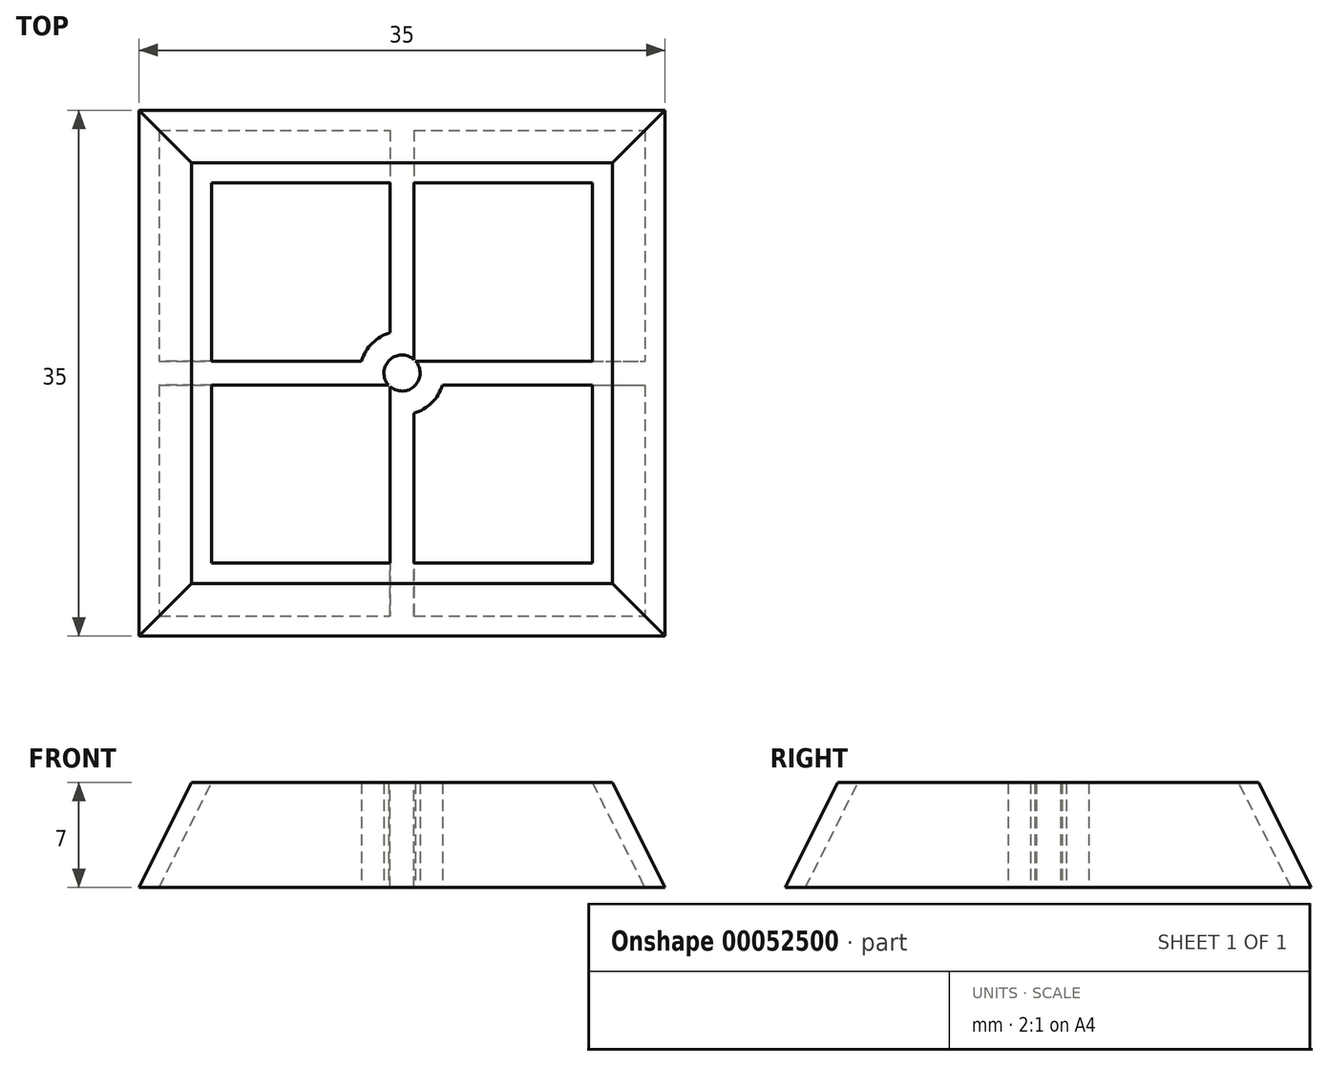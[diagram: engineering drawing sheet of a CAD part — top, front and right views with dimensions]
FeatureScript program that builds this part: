
annotation { "Feature Type Name" : "Feature", "Feature Type Description" : "" }
export const myFeature = defineFeature(function(context is Context, id is Id, definition is map)
    precondition{}
    {
        {
            var Q0;
            Q0=qCreatedBy(makeId("Top.planeOp"),FACE);
            var sketch = newSketch(context, id + "F0", { "sketchPlane" : qUnion([Q0])});
            skLineSegment(sketch, "E0.rect.bottom", {"start": v(-17.5, 17.5) * mm, "end": v(17.5, 17.5) * mm});
            skLineSegment(sketch, "E0.rect.top", {"start": v(-17.5, -17.5) * mm, "end": v(17.5, -17.5) * mm});
            skLineSegment(sketch, "E0.rect.left", {"start": v(-17.5, 17.5) * mm, "end": v(-17.5, -17.5) * mm});
            skLineSegment(sketch, "E0.rect.right", {"start": v(17.5, 17.5) * mm, "end": v(17.5, -17.5) * mm});
            skPoint(sketch, "E0.rect.middle", {"position": v(0, 0) * mm});
            skSolve(sketch);
        }
        {
            var Q0;
            Q0=qCreatedBy(makeId("Top.planeOp"),FACE);
            cPlane(context, id + "F1", {"entities" : qUnion([Q0]), "cplaneType" : CPlaneType.OFFSET, "offset" : 7 * mm, "width" : 150 * mm, "height" : 150 * mm});
        }
        {
            var Q0;
            Q0=qCreatedBy(id+"F1.planeOp",FACE);
            var sketch = newSketch(context, id + "F2", { "sketchPlane" : qUnion([Q0])});
            skLineSegment(sketch, "E1.rect.bottom", {"start": v(14, -14) * mm, "end": v(-14, -14) * mm});
            skLineSegment(sketch, "E1.rect.top", {"start": v(14, 14) * mm, "end": v(-14, 14) * mm});
            skLineSegment(sketch, "E1.rect.left", {"start": v(14, -14) * mm, "end": v(14, 14) * mm});
            skLineSegment(sketch, "E1.rect.right", {"start": v(-14, -14) * mm, "end": v(-14, 14) * mm});
            skPoint(sketch, "E1.rect.middle", {"position": v(0, 0) * mm});
            skSolve(sketch);
        }
        {
            var Q0;
            Q0=makeQuery(id+"F0.imprint","IMPRINT",FACE,{"disambiguationData":[TD([[makeQuery(id+"F0.imprint","IMPRINT",EDGE,{"derivedFrom":sQuery(id+"F0.wireOp",EDGE,"E0.rect.bottom")}),-1.0]])]});
            var Q1;
            Q1=makeQuery(id+"F2.imprint","IMPRINT",FACE,{"disambiguationData":[TD([[makeQuery(id+"F2.imprint","IMPRINT",EDGE,{"derivedFrom":sQuery(id+"F2.wireOp",EDGE,"E1.rect.bottom")}),-1.0]])]});
            loft(context, id + "F3", {"sheetProfilesArray" : [{ "sheetProfileEntities" : qUnion([Q0]) }, { "sheetProfileEntities" : qUnion([Q1]) }]});
        }
        {
            var Q0;
            Q0=makeQuery(id+"F3.opLoft","CAP_FACE",FACE,{"disambiguationData":[OSD([makeQuery(id+"F2.imprint","IMPRINT",FACE,{"disambiguationData":[TD([[makeQuery(id+"F2.imprint","IMPRINT",EDGE,{"derivedFrom":sQuery(id+"F2.wireOp",EDGE,"E1.rect.bottom")}),-1.0]])]})])],"isStart":true});
            var Q1;
            Q1=makeQuery(id+"F3.opLoft","CAP_FACE",FACE,{"disambiguationData":[OSD([makeQuery(id+"F0.imprint","IMPRINT",FACE,{"disambiguationData":[TD([[makeQuery(id+"F0.imprint","IMPRINT",EDGE,{"derivedFrom":sQuery(id+"F0.wireOp",EDGE,"E0.rect.bottom")}),-1.0]])]})])],"isStart":true});
            shell(context, id + "F4", {"entities" : qUnion([Q0, Q1]), "thickness" : 1.2 * mm});
        }
        {
            var Q0;
            Q0=qCreatedBy(makeId("Top.planeOp"),FACE);
            var sketch = newSketch(context, id + "F5", { "sketchPlane" : qUnion([Q0])});
            skLineSegment(sketch, "E2.0", {"start": v(17.5, 17.5) * mm, "end": v(-17.5, 17.5) * mm, "construction": true});
            skLineSegment(sketch, "E2.1", {"start": v(-17.5, -17.5) * mm, "end": v(17.5, -17.5) * mm, "construction": true});
            skLineSegment(sketch, "E2.2", {"start": v(17.5, -17.5) * mm, "end": v(17.5, 17.5) * mm, "construction": true});
            skLineSegment(sketch, "E2.3", {"start": v(-17.5, 17.5) * mm, "end": v(-17.5, -17.5) * mm, "construction": true});
            skCircle(sketch, "E3", {"center": v(0, 0) * mm, "radius": 1.2 * mm});
            skCircle(sketch, "E4.0", {"center": v(0, 0) * mm, "radius": 2.8 * mm});
            skLineSegment(sketch, "E5", {"start": v(0, 17.5) * mm, "end": v(0, -17.5) * mm, "construction": true});
            skLineSegment(sketch, "E6", {"start": v(-17.5, 0) * mm, "end": v(17.5, 0) * mm, "construction": true});
            skLineSegment(sketch, "E7", {"start": v(-0.8, 16.2) * mm, "end": v(-0.8, -16.2) * mm});
            skLineSegment(sketch, "E8.MirrorCS", {"start": v(0.8, 16.2) * mm, "end": v(0.8, -16.2) * mm});
            skLineSegment(sketch, "E9", {"start": v(-16.2, -0.8) * mm, "end": v(16.2, -0.8) * mm});
            skLineSegment(sketch, "E10.MirrorCS", {"start": v(-16.2, 0.8) * mm, "end": v(16.2, 0.8) * mm});
            skLineSegment(sketch, "E11", {"start": v(-17.5, 0.8) * mm, "end": v(-17.5, -0.8) * mm});
            skLineSegment(sketch, "E12", {"start": v(17.5, 0.8) * mm, "end": v(17.5, -0.8) * mm});
            skLineSegment(sketch, "E13", {"start": v(-0.8, -17.5) * mm, "end": v(0.8, -17.5) * mm});
            skLineSegment(sketch, "E14", {"start": v(-0.8, 17.5) * mm, "end": v(0.8, 17.5) * mm});
            skLineSegment(sketch, "E15.rect.bottom", {"start": v(-16.2, 16.2) * mm, "end": v(16.2, 16.2) * mm, "construction": true});
            skLineSegment(sketch, "E15.rect.top", {"start": v(-16.2, -16.2) * mm, "end": v(16.2, -16.2) * mm, "construction": true});
            skLineSegment(sketch, "E15.rect.left", {"start": v(-16.2, 16.2) * mm, "end": v(-16.2, -16.2) * mm, "construction": true});
            skLineSegment(sketch, "E15.rect.right", {"start": v(16.2, 16.2) * mm, "end": v(16.2, -16.2) * mm, "construction": true});
            skLineSegment(sketch, "E16", {"start": v(-0.8, -16.2) * mm, "end": v(0.8, -16.2) * mm});
            skLineSegment(sketch, "E17", {"start": v(16.2, 0.8) * mm, "end": v(16.2, -0.8) * mm});
            skLineSegment(sketch, "E18", {"start": v(-0.8, 16.2) * mm, "end": v(0.8, 16.2) * mm});
            skLineSegment(sketch, "E19", {"start": v(-16.2, -0.8) * mm, "end": v(-16.2, 0.8) * mm});
            skSolve(sketch);
        }
        {
            var Q0;
            {var subQ5=sQuery(id+"F5.wireOp",EDGE,"E19");Q0=makeQuery(id+"F5.imprint","IMPRINT",FACE,{"disambiguationData":[TD([[makeQuery(id+"F5.imprint","IMPRINT",EDGE,{"derivedFrom":subQ5}),-1.0]])]});}
            var Q1;
            {var subQ0=sQuery(id+"F5.wireOp",EDGE,"E10.MirrorCS");var subQ1=sQuery(id+"F5.wireOp",EDGE,"E3");var subQ2=makeQuery(id+"F5.imprint","INTERSECT",VERTEX,{"disambiguationData":[OD(1.0)],"derivedFrom":[subQ1,subQ0]});Q1=makeQuery(id+"F5.imprint","IMPRINT",FACE,{"disambiguationData":[TD([[makeQuery(id+"F5.imprint","IMPRINT",EDGE,{"disambiguationData":[TD([[subQ2,-1.0]])],"derivedFrom":subQ1}),-1.0]])]});}
            var Q2;
            {var subQ0=sQuery(id+"F5.wireOp",EDGE,"E7");var subQ1=sQuery(id+"F5.wireOp",EDGE,"E3");var subQ2=makeQuery(id+"F5.imprint","INTERSECT",VERTEX,{"disambiguationData":[OD(0.0)],"derivedFrom":[subQ1,subQ0]});Q2=makeQuery(id+"F5.imprint","IMPRINT",FACE,{"disambiguationData":[TD([[makeQuery(id+"F5.imprint","IMPRINT",EDGE,{"disambiguationData":[TD([[subQ2,-1.0]])],"derivedFrom":subQ1}),-1.0]])]});}
            var Q3;
            {var subQ0=sQuery(id+"F5.wireOp",EDGE,"E8.MirrorCS");var subQ1=sQuery(id+"F5.wireOp",EDGE,"E3");var subQ2=makeQuery(id+"F5.imprint","INTERSECT",VERTEX,{"disambiguationData":[OD(0.0)],"derivedFrom":[subQ1,subQ0]});Q3=makeQuery(id+"F5.imprint","IMPRINT",FACE,{"disambiguationData":[TD([[makeQuery(id+"F5.imprint","IMPRINT",EDGE,{"disambiguationData":[TD([[subQ2,-1.0]])],"derivedFrom":subQ1}),-1.0]])]});}
            var Q4;
            {var subQ5=sQuery(id+"F5.wireOp",EDGE,"E18");Q4=makeQuery(id+"F5.imprint","IMPRINT",FACE,{"disambiguationData":[TD([[makeQuery(id+"F5.imprint","IMPRINT",EDGE,{"derivedFrom":subQ5}),-1.0]])]});}
            var Q5;
            {var subQ0=sQuery(id+"F5.wireOp",EDGE,"E8.MirrorCS");var subQ1=sQuery(id+"F5.wireOp",EDGE,"E3");var subQ2=makeQuery(id+"F5.imprint","INTERSECT",VERTEX,{"disambiguationData":[OD(0.0)],"derivedFrom":[subQ1,subQ0]});Q5=makeQuery(id+"F5.imprint","IMPRINT",FACE,{"disambiguationData":[TD([[makeQuery(id+"F5.imprint","IMPRINT",EDGE,{"disambiguationData":[TD([[subQ2,1.0]])],"derivedFrom":subQ1}),-1.0]])]});}
            var Q6;
            {var subQ0=sQuery(id+"F5.wireOp",EDGE,"E10.MirrorCS");var subQ1=sQuery(id+"F5.wireOp",EDGE,"E3");var subQ2=makeQuery(id+"F5.imprint","INTERSECT",VERTEX,{"disambiguationData":[OD(0.0)],"derivedFrom":[subQ1,subQ0]});Q6=makeQuery(id+"F5.imprint","IMPRINT",FACE,{"disambiguationData":[TD([[makeQuery(id+"F5.imprint","IMPRINT",EDGE,{"disambiguationData":[TD([[subQ2,1.0]])],"derivedFrom":subQ1}),-1.0]])]});}
            var Q7;
            {var subQ5=sQuery(id+"F5.wireOp",EDGE,"E17");Q7=makeQuery(id+"F5.imprint","IMPRINT",FACE,{"disambiguationData":[TD([[makeQuery(id+"F5.imprint","IMPRINT",EDGE,{"derivedFrom":subQ5}),-1.0]])]});}
            var Q8;
            {var subQ0=sQuery(id+"F5.wireOp",EDGE,"E8.MirrorCS");var subQ1=sQuery(id+"F5.wireOp",EDGE,"E3");var subQ2=makeQuery(id+"F5.imprint","INTERSECT",VERTEX,{"disambiguationData":[OD(1.0)],"derivedFrom":[subQ1,subQ0]});Q8=makeQuery(id+"F5.imprint","IMPRINT",FACE,{"disambiguationData":[TD([[makeQuery(id+"F5.imprint","IMPRINT",EDGE,{"disambiguationData":[TD([[subQ2,-1.0]])],"derivedFrom":subQ1}),-1.0]])]});}
            var Q9;
            {var subQ0=sQuery(id+"F5.wireOp",EDGE,"E9");var subQ1=sQuery(id+"F5.wireOp",EDGE,"E3");var subQ2=makeQuery(id+"F5.imprint","INTERSECT",VERTEX,{"disambiguationData":[OD(0.0)],"derivedFrom":[subQ1,subQ0]});Q9=makeQuery(id+"F5.imprint","IMPRINT",FACE,{"disambiguationData":[TD([[makeQuery(id+"F5.imprint","IMPRINT",EDGE,{"disambiguationData":[TD([[subQ2,-1.0]])],"derivedFrom":subQ1}),-1.0]])]});}
            var Q10;
            {var subQ0=sQuery(id+"F5.wireOp",EDGE,"E7");var subQ1=sQuery(id+"F5.wireOp",EDGE,"E3");var subQ2=makeQuery(id+"F5.imprint","INTERSECT",VERTEX,{"disambiguationData":[OD(1.0)],"derivedFrom":[subQ1,subQ0]});Q10=makeQuery(id+"F5.imprint","IMPRINT",FACE,{"disambiguationData":[TD([[makeQuery(id+"F5.imprint","IMPRINT",EDGE,{"disambiguationData":[TD([[subQ2,-1.0]])],"derivedFrom":subQ1}),-1.0]])]});}
            var Q11;
            {var subQ5=sQuery(id+"F5.wireOp",EDGE,"E16");Q11=makeQuery(id+"F5.imprint","IMPRINT",FACE,{"disambiguationData":[TD([[makeQuery(id+"F5.imprint","IMPRINT",EDGE,{"derivedFrom":subQ5}),1.0]])]});}
            var Q12;
            Q12=makeQuery(id+"F3.opLoft","CAP_FACE",FACE,{"disambiguationData":[OSD([makeQuery(id+"F2.imprint","IMPRINT",FACE,{"disambiguationData":[TD([[makeQuery(id+"F2.imprint","IMPRINT",EDGE,{"derivedFrom":sQuery(id+"F2.wireOp",EDGE,"E1.rect.bottom")}),-1.0]])]})])],"isStart":true});
            extrude(context, id + "F6", {"entities" : qUnion([Q0, Q1, Q2, Q3, Q4, Q5, Q6, Q7, Q8, Q9, Q10, Q11]), "endBound" : BoundingType.UP_TO_SURFACE, "endBoundEntityFace" : qUnion([Q12]), "depth" : 8.93 * mm});
        }
        {
            var Q0;
            Q0=makeQuery(id+"F6.opExtrude","CAP_EDGE",EDGE,{"disambiguationData":[OSD([sQuery(id+"F5.wireOp",EDGE,"E19")])],"isStart":false});
            var Q1;
            Q1=makeQuery(id+"F6.opExtrude","CAP_EDGE",EDGE,{"disambiguationData":[OSD([sQuery(id+"F5.wireOp",EDGE,"E18")])],"isStart":false});
            var Q2;
            Q2=makeQuery(id+"F6.opExtrude","CAP_EDGE",EDGE,{"disambiguationData":[OSD([sQuery(id+"F5.wireOp",EDGE,"E17")])],"isStart":false});
            var Q3;
            Q3=makeQuery(id+"F6.opExtrude","CAP_EDGE",EDGE,{"disambiguationData":[OSD([sQuery(id+"F5.wireOp",EDGE,"E16")])],"isStart":false});
            chamfer(context, id + "F7", {"entities" : qUnion([Q0, Q1, Q2, Q3]), "chamferType" : ChamferType.TWO_OFFSETS, "width1" : 6 * mm, "oppositeDirection" : false, "width2" : 3 * mm, "tangentPropagation" : true});
        }
        {
            var Q0;
            Q0=makeQuery(id+"F3.opLoft","SWEPT_BODY",BODY,{"disambiguationData":[OSD([makeQuery(id+"F0.imprint","IMPRINT",FACE,{"disambiguationData":[TD([[makeQuery(id+"F0.imprint","IMPRINT",EDGE,{"derivedFrom":sQuery(id+"F0.wireOp",EDGE,"E0.rect.bottom")}),-1.0]])]}),makeQuery(id+"F2.imprint","IMPRINT",FACE,{"disambiguationData":[TD([[makeQuery(id+"F2.imprint","IMPRINT",EDGE,{"derivedFrom":sQuery(id+"F2.wireOp",EDGE,"E1.rect.bottom")}),-1.0]])]})])]});
            var Q1;
            Q1=makeQuery(id+"F6.opExtrude","SWEPT_BODY",BODY,{"disambiguationData":[OSD([sQuery(id+"F5.wireOp",EDGE,"E3"),sQuery(id+"F5.wireOp",EDGE,"E4.0"),sQuery(id+"F5.wireOp",EDGE,"E7"),sQuery(id+"F5.wireOp",EDGE,"E8.MirrorCS"),sQuery(id+"F5.wireOp",EDGE,"E9"),sQuery(id+"F5.wireOp",EDGE,"E10.MirrorCS"),sQuery(id+"F5.wireOp",EDGE,"E16"),sQuery(id+"F5.wireOp",EDGE,"E17"),sQuery(id+"F5.wireOp",EDGE,"E18"),sQuery(id+"F5.wireOp",EDGE,"E19")])]});
            booleanBodies(context, id + "F8", {"operationType" : BooleanOperationType.UNION, "tools" : qUnion([Q0, Q1])});
        }
    });
